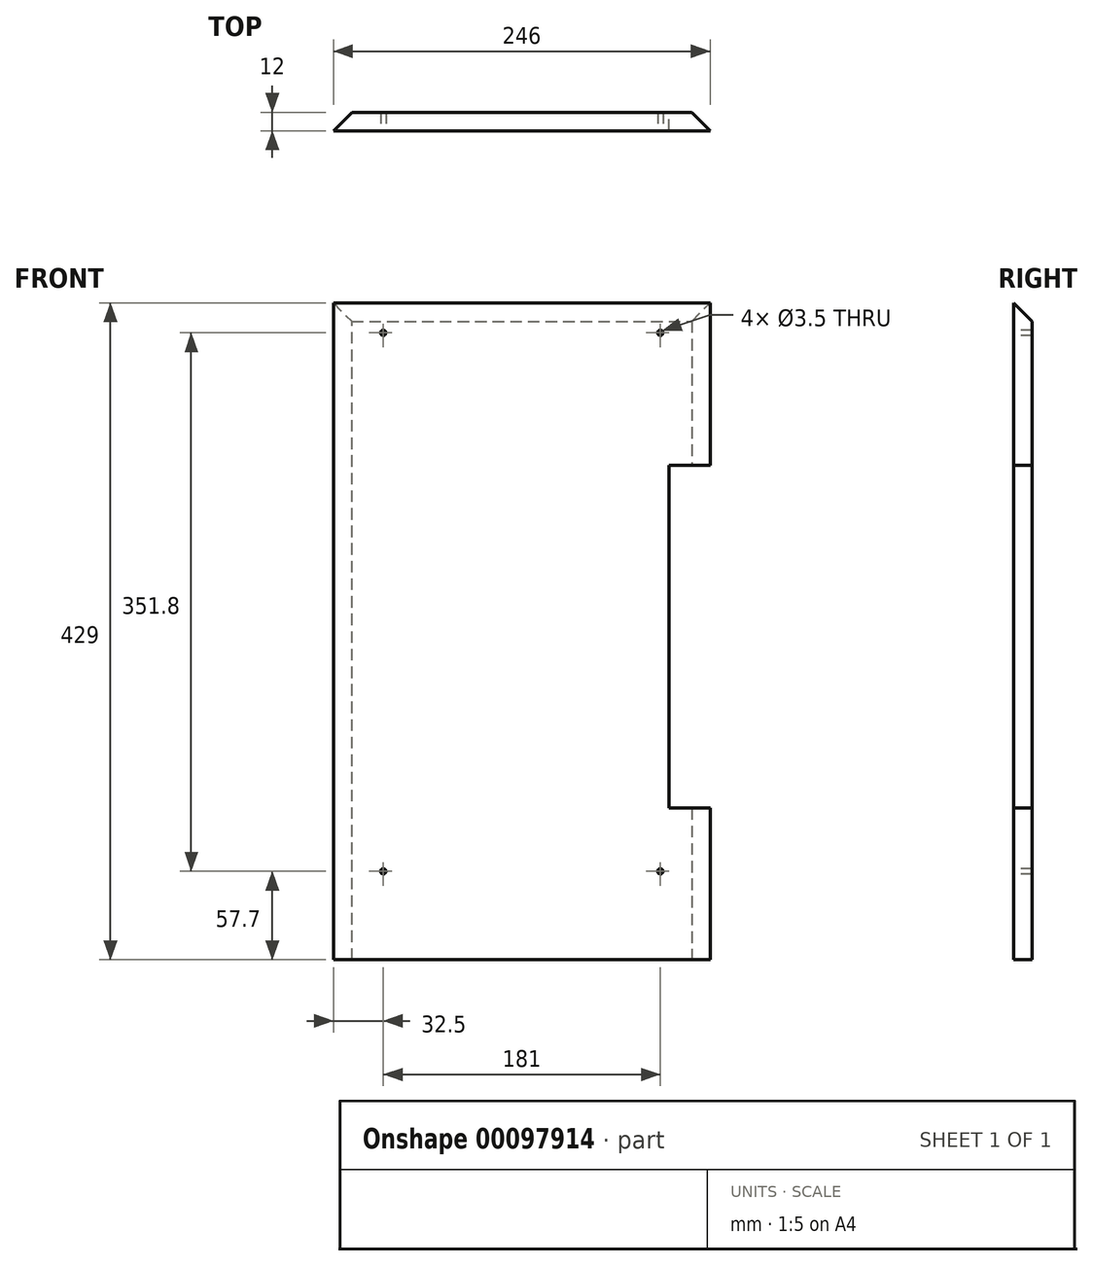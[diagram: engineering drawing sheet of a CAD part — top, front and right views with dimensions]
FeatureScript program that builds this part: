
annotation { "Feature Type Name" : "Feature", "Feature Type Description" : "" }
export const myFeature = defineFeature(function(context is Context, id is Id, definition is map)
    precondition{}
    {
        {
            var Q0;
            Q0=qCreatedBy(makeId("Front.planeOp"),FACE);
            var sketch = newSketch(context, id + "F0", { "sketchPlane" : qUnion([Q0])});
            skLineSegment(sketch, "E0.bottom", {"start": v(-123, 214.5) * mm, "end": v(123, 214.5) * mm});
            skLineSegment(sketch, "E0.top", {"start": v(-123, -214.5) * mm, "end": v(123, -214.5) * mm});
            skLineSegment(sketch, "E0.left", {"start": v(-123, 214.5) * mm, "end": v(-123, -214.5) * mm});
            skLineSegment(sketch, "E0.right", {"start": v(123, 214.5) * mm, "end": v(123, -214.5) * mm});
            skSolve(sketch);
        }
        {
            var Q0;
            Q0=makeQuery(id+"F0.imprint","IMPRINT",FACE,{"disambiguationData":[TD([[makeQuery(id+"F0.imprint","IMPRINT",EDGE,{"derivedFrom":sQuery(id+"F0.wireOp",EDGE,"E0.bottom")}),-1.0]])]});
            extrude(context, id + "F1", {"entities" : qUnion([Q0]), "depth" : 12 * mm});
        }
        {
            var Q0;
            Q0=makeQuery(id+"F1.opExtrude","CAP_FACE",FACE,{"disambiguationData":[OSD([sQuery(id+"F0.wireOp",EDGE,"E0.bottom"),sQuery(id+"F0.wireOp",EDGE,"E0.top"),sQuery(id+"F0.wireOp",EDGE,"E0.left"),sQuery(id+"F0.wireOp",EDGE,"E0.right")])],"isStart":true});
            var sketch = newSketch(context, id + "F2", { "sketchPlane" : qUnion([Q0])});
            skLineSegment(sketch, "E1.bottom", {"start": v(-123, 108.5) * mm, "end": v(-96, 108.5) * mm});
            skLineSegment(sketch, "E1.top", {"start": v(-123, -115.5) * mm, "end": v(-96, -115.5) * mm});
            skLineSegment(sketch, "E1.left", {"start": v(-123, 108.5) * mm, "end": v(-123, -115.5) * mm});
            skLineSegment(sketch, "E1.right", {"start": v(-96, 108.5) * mm, "end": v(-96, -115.5) * mm});
            skSolve(sketch);
        }
        {
            var Q0;
            Q0=makeQuery(id+"F2.imprint","IMPRINT",FACE,{"disambiguationData":[TD([[makeQuery(id+"F2.imprint","IMPRINT",EDGE,{"derivedFrom":sQuery(id+"F2.wireOp",EDGE,"E1.bottom")}),-1.0]])]});
            extrude(context, id + "F3", {"entities" : qUnion([Q0]), "operationType" : NewBodyOperationType.REMOVE, "oppositeDirection" : true, "depth" : 25 * mm});
        }
        {
            var Q0;
            Q0=makeQuery(id+"F1.opExtrude","CAP_EDGE",EDGE,{"disambiguationData":[OSD([sQuery(id+"F0.wireOp",EDGE,"E0.bottom")])],"isStart":true});
            var Q1;
            Q1=makeQuery(id+"F1.opExtrude","CAP_EDGE",EDGE,{"disambiguationData":[OSD([sQuery(id+"F0.wireOp",EDGE,"E0.left")])],"isStart":true});
            var Q2;
            {var subQ0=sQuery(id+"F0.wireOp",EDGE,"E0.bottom");var subQ1=sQuery(id+"F0.wireOp",EDGE,"E0.right");Q2=makeQuery(id+"F3.boolean.opBoolean","SPLIT",EDGE,{"disambiguationData":[TD([makeQuery(id+"F1.opExtrude","SWEPT_FACE",FACE,{"disambiguationData":[OSD([subQ0])]})])],"derivedFrom":makeQuery(id+"F1.opExtrude","CAP_EDGE",EDGE,{"disambiguationData":[OSD([subQ1])],"isStart":true})});}
            var Q3;
            {var subQ0=sQuery(id+"F0.wireOp",EDGE,"E0.right");var subQ1=sQuery(id+"F0.wireOp",EDGE,"E0.top");Q3=makeQuery(id+"F3.boolean.opBoolean","SPLIT",EDGE,{"disambiguationData":[TD([makeQuery(id+"F1.opExtrude","SWEPT_FACE",FACE,{"disambiguationData":[OSD([subQ1])]})])],"derivedFrom":makeQuery(id+"F1.opExtrude","CAP_EDGE",EDGE,{"disambiguationData":[OSD([subQ0])],"isStart":true})});}
            chamfer(context, id + "F4", {"entities" : qUnion([Q0, Q1, Q2, Q3]), "width" : 12 * mm, "tangentPropagation" : true});
        }
        {
            var Q0;
            Q0=makeQuery(id+"F1.opExtrude","CAP_FACE",FACE,{"disambiguationData":[OSD([sQuery(id+"F0.wireOp",EDGE,"E0.bottom"),sQuery(id+"F0.wireOp",EDGE,"E0.top"),sQuery(id+"F0.wireOp",EDGE,"E0.left"),sQuery(id+"F0.wireOp",EDGE,"E0.right")])],"isStart":false});
            var sketch = newSketch(context, id + "F5", { "sketchPlane" : qUnion([Q0])});
            skLineSegment(sketch, "E2.0", {"start": v(103.5, -115.5) * mm, "end": v(103.5, -195) * mm, "construction": true});
            skLineSegment(sketch, "E2.1", {"start": v(103.5, 195) * mm, "end": v(103.5, 108.5) * mm, "construction": true});
            skLineSegment(sketch, "E2.2", {"start": v(-103.5, 195) * mm, "end": v(103.5, 195) * mm, "construction": true});
            skLineSegment(sketch, "E2.3", {"start": v(-103.5, 195) * mm, "end": v(-103.5, -195) * mm, "construction": true});
            skLineSegment(sketch, "E2.4", {"start": v(-103.5, -195) * mm, "end": v(103.5, -195) * mm, "construction": true});
            skLineSegment(sketch, "E3.0", {"start": v(90.5, -115.5) * mm, "end": v(90.5, -182) * mm, "construction": true});
            skLineSegment(sketch, "E3.1", {"start": v(90.5, 182) * mm, "end": v(90.5, 108.5) * mm, "construction": true});
            skLineSegment(sketch, "E3.2", {"start": v(-90.5, 182) * mm, "end": v(90.5, 182) * mm, "construction": true});
            skLineSegment(sketch, "E3.3", {"start": v(-90.5, 182) * mm, "end": v(-90.5, -182) * mm, "construction": true});
            skLineSegment(sketch, "E3.4", {"start": v(-90.5, -182) * mm, "end": v(90.5, -182) * mm, "construction": true});
            skPoint(sketch, "E4", {"position": v(-90.5, 195) * mm});
            skPoint(sketch, "E5", {"position": v(90.5, 195) * mm});
            skLineSegment(sketch, "E6", {"start": v(-90.5, -156.8) * mm, "end": v(90.5, -156.8) * mm, "construction": true});
            skSolve(sketch);
        }
        {
            var Q0;
            Q0=sQuery(id+"F5.wireOp",VERTEX,"E4");
            var Q1;
            Q1=sQuery(id+"F5.wireOp",VERTEX,"E5");
            var Q2;
            Q2=sQuery(id+"F5.wireOp",VERTEX,"E6.end");
            var Q3;
            Q3=sQuery(id+"F5.wireOp",VERTEX,"E6.start");
            var Q4;
            Q4=makeQuery(id+"F1.opExtrude","SWEPT_BODY",BODY,{"disambiguationData":[OSD([sQuery(id+"F0.wireOp",EDGE,"E0.bottom"),sQuery(id+"F0.wireOp",EDGE,"E0.top"),sQuery(id+"F0.wireOp",EDGE,"E0.left"),sQuery(id+"F0.wireOp",EDGE,"E0.right")])]});
            hole(context, id + "F6", {"style" : HoleStyle.SIMPLE, "endStyle" : HoleEndStyle.THROUGH, "holeDiameter" : 3.5 * mm, "locations" : qUnion([Q0, Q1, Q2, Q3]), "scope" : qUnion([Q4]), "isTappedThrough" : true});
        }
    });
